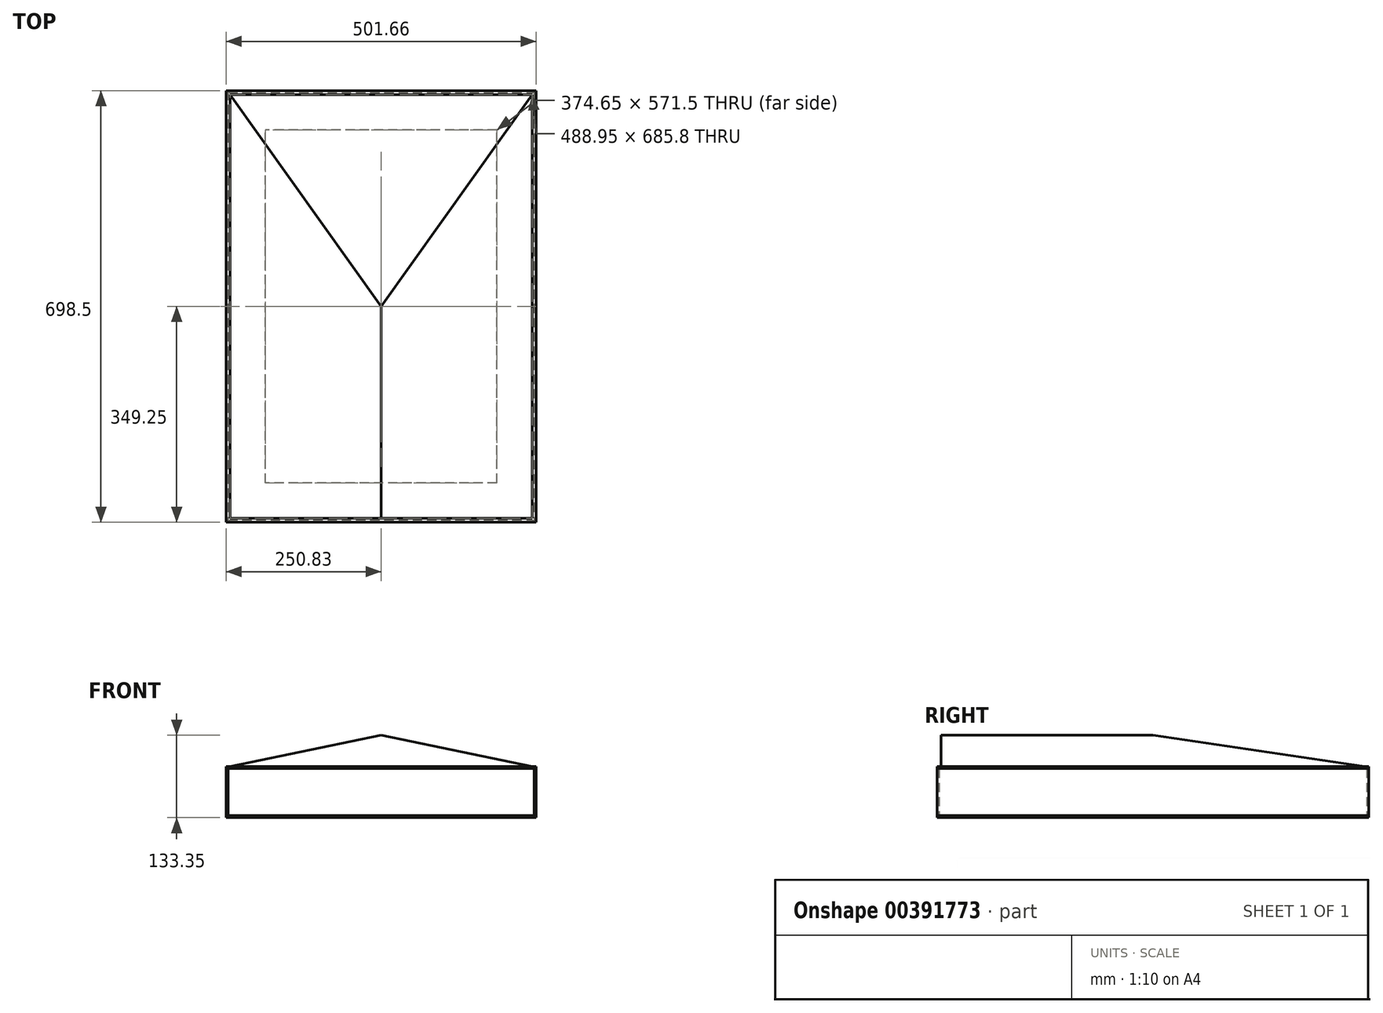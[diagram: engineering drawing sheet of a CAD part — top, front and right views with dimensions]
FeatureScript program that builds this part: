
annotation { "Feature Type Name" : "Feature", "Feature Type Description" : "" }
export const myFeature = defineFeature(function(context is Context, id is Id, definition is map)
    precondition{}
    {
        {
            var Q0;
            Q0=qCreatedBy(makeId("Top.planeOp"),FACE);
            var sketch = newSketch(context, id + "F0", { "sketchPlane" : qUnion([Q0])});
            skLineSegment(sketch, "E0.bottom", {"start": v(225.42, -323.85) * mm, "end": v(-225.43, -323.85) * mm});
            skLineSegment(sketch, "E0.top", {"start": v(225.43, 323.85) * mm, "end": v(-225.42, 323.85) * mm});
            skLineSegment(sketch, "E0.left", {"start": v(225.42, -323.85) * mm, "end": v(225.43, 323.85) * mm});
            skLineSegment(sketch, "E0.right", {"start": v(-225.43, -323.85) * mm, "end": v(-225.42, 323.85) * mm});
            skPoint(sketch, "E0.middle", {"position": v(0, 0) * mm});
            skLineSegment(sketch, "E1.0", {"start": v(-187.33, -285.75) * mm, "end": v(-187.32, 285.75) * mm});
            skLineSegment(sketch, "E1.1", {"start": v(187.32, -285.75) * mm, "end": v(-187.33, -285.75) * mm});
            skLineSegment(sketch, "E1.2", {"start": v(187.32, -285.75) * mm, "end": v(187.33, 285.75) * mm});
            skLineSegment(sketch, "E1.3", {"start": v(187.33, 285.75) * mm, "end": v(-187.32, 285.75) * mm});
            skLineSegment(sketch, "E2.0", {"start": v(-250.83, -349.25) * mm, "end": v(-250.83, 349.25) * mm});
            skLineSegment(sketch, "E2.1", {"start": v(250.83, -349.25) * mm, "end": v(-250.83, -349.25) * mm});
            skLineSegment(sketch, "E2.2", {"start": v(250.83, -349.25) * mm, "end": v(250.83, 349.25) * mm});
            skLineSegment(sketch, "E2.3", {"start": v(250.83, 349.25) * mm, "end": v(-250.83, 349.25) * mm});
            skSolve(sketch);
        }
        {
            var Q0;
            Q0 = qSketchRegion(id + "Ful7OC0vkHjbYUr_0", true);
            var Q1;
            Q1=makeQuery(id+"F0.imprint","IMPRINT",FACE,{"disambiguationData":[TD([[makeQuery(id+"F0.imprint","IMPRINT",EDGE,{"derivedFrom":sQuery(id+"F0.wireOp",EDGE,"E0.bottom")}),1.0]])]});
            var Q2;
            Q2=makeQuery(id+"F0.imprint","IMPRINT",FACE,{"disambiguationData":[TD([[makeQuery(id+"F0.imprint","IMPRINT",EDGE,{"derivedFrom":sQuery(id+"F0.wireOp",EDGE,"E0.bottom")}),-1.0]])]});
            extrude(context, id + "F1", {"entities" : qUnion([Q0, Q1, Q2]), "depth" : 3.17 * mm});
        }
        {
            var Q0;
            Q0=makeQuery(id+"F1.opExtrude","CAP_FACE",FACE,{"disambiguationData":[OSD([sQuery(id+"F0.wireOp",EDGE,"E1.0"),sQuery(id+"F0.wireOp",EDGE,"E1.1"),sQuery(id+"F0.wireOp",EDGE,"E1.2"),sQuery(id+"F0.wireOp",EDGE,"E1.3"),sQuery(id+"F0.wireOp",EDGE,"E2.0"),sQuery(id+"F0.wireOp",EDGE,"E2.1"),sQuery(id+"F0.wireOp",EDGE,"E2.2"),sQuery(id+"F0.wireOp",EDGE,"E2.3")])],"isStart":false});
            var sketch = newSketch(context, id + "F2", { "sketchPlane" : qUnion([Q0])});
            skLineSegment(sketch, "E3.bottom", {"start": v(-250.83, 349.25) * mm, "end": v(-247.65, 349.25) * mm});
            skLineSegment(sketch, "E3.top", {"start": v(-250.83, -349.25) * mm, "end": v(-247.65, -349.25) * mm});
            skLineSegment(sketch, "E3.left", {"start": v(-250.83, 349.25) * mm, "end": v(-250.83, -349.25) * mm});
            skLineSegment(sketch, "E3.right", {"start": v(-247.65, 349.25) * mm, "end": v(-247.65, -349.25) * mm});
            skSolve(sketch);
        }
        {
            var Q0;
            Q0 = qSketchRegion(id + "F2", true);
            extrude(context, id + "F3", {"entities" : qUnion([Q0]), "depth" : 76.2 * mm});
        }
        {
            var Q0;
            Q0=makeQuery(id+"F3.opExtrude","SWEPT_BODY",BODY,{"disambiguationData":[OSD([sQuery(id+"F2.wireOp",EDGE,"E3.bottom"),sQuery(id+"F2.wireOp",EDGE,"E3.top"),sQuery(id+"F2.wireOp",EDGE,"E3.left"),sQuery(id+"F2.wireOp",EDGE,"E3.right")])]});
            var Q1;
            Q1=qCreatedBy(makeId("Right.planeOp"),FACE);
            mirror(context, id + "F4", {"entities" : qUnion([Q0]), "mirrorPlane" : qUnion([Q1])});
        }
        {
            var Q0;
            Q0=makeQuery(id+"F1.opExtrude","CAP_FACE",FACE,{"disambiguationData":[OSD([sQuery(id+"F0.wireOp",EDGE,"E1.0"),sQuery(id+"F0.wireOp",EDGE,"E1.1"),sQuery(id+"F0.wireOp",EDGE,"E1.2"),sQuery(id+"F0.wireOp",EDGE,"E1.3"),sQuery(id+"F0.wireOp",EDGE,"E2.0"),sQuery(id+"F0.wireOp",EDGE,"E2.1"),sQuery(id+"F0.wireOp",EDGE,"E2.2"),sQuery(id+"F0.wireOp",EDGE,"E2.3")])],"isStart":false});
            var sketch = newSketch(context, id + "F5", { "sketchPlane" : qUnion([Q0])});
            skLineSegment(sketch, "E4.bottom", {"start": v(-247.65, -349.25) * mm, "end": v(247.65, -349.25) * mm});
            skLineSegment(sketch, "E4.top", {"start": v(-247.65, -346.08) * mm, "end": v(247.65, -346.08) * mm});
            skLineSegment(sketch, "E4.left", {"start": v(-247.65, -349.25) * mm, "end": v(-247.65, -346.08) * mm});
            skLineSegment(sketch, "E4.right", {"start": v(247.65, -349.25) * mm, "end": v(247.65, -346.08) * mm});
            skSolve(sketch);
        }
        {
            var Q0;
            Q0 = qSketchRegion(id + "F5", true);
            var Q1;
            Q1=makeQuery(id+"F4.opPattern","COPY",FACE,{"derivedFrom":makeQuery(id+"F3.opExtrude","CAP_FACE",FACE,{"disambiguationData":[OSD([sQuery(id+"F2.wireOp",EDGE,"E3.bottom"),sQuery(id+"F2.wireOp",EDGE,"E3.top"),sQuery(id+"F2.wireOp",EDGE,"E3.left"),sQuery(id+"F2.wireOp",EDGE,"E3.right")])],"isStart":false}),"instanceName":"1"});
            extrude(context, id + "F6", {"entities" : qUnion([Q0]), "endBound" : BoundingType.UP_TO_SURFACE, "endBoundEntityFace" : qUnion([Q1]), "depth" : 25.4 * mm});
        }
        {
            var Q0;
            Q0=makeQuery(id+"F6.opExtrude","SWEPT_BODY",BODY,{"disambiguationData":[OSD([sQuery(id+"F5.wireOp",EDGE,"E4.bottom"),sQuery(id+"F5.wireOp",EDGE,"E4.top"),sQuery(id+"F5.wireOp",EDGE,"E4.left"),sQuery(id+"F5.wireOp",EDGE,"E4.right")])]});
            var Q1;
            Q1=qCreatedBy(makeId("Front.planeOp"),FACE);
            mirror(context, id + "F7", {"entities" : qUnion([Q0]), "mirrorPlane" : qUnion([Q1])});
        }
        {
            var Q0;
            Q0=makeQuery(id+"F3.opExtrude","CAP_FACE",FACE,{"disambiguationData":[OSD([sQuery(id+"F2.wireOp",EDGE,"E3.bottom"),sQuery(id+"F2.wireOp",EDGE,"E3.top"),sQuery(id+"F2.wireOp",EDGE,"E3.left"),sQuery(id+"F2.wireOp",EDGE,"E3.right")])],"isStart":false});
            var sketch = newSketch(context, id + "F8", { "sketchPlane" : qUnion([Q0])});
            skLineSegment(sketch, "E5.bottom", {"start": v(-250.83, -349.25) * mm, "end": v(250.82, -349.25) * mm});
            skLineSegment(sketch, "E5.top", {"start": v(-250.83, 349.25) * mm, "end": v(250.83, 349.25) * mm});
            skLineSegment(sketch, "E5.left", {"start": v(-250.83, -349.25) * mm, "end": v(-250.83, 349.25) * mm});
            skLineSegment(sketch, "E5.right", {"start": v(250.83, -349.25) * mm, "end": v(250.83, 349.25) * mm});
            skLineSegment(sketch, "E6.bottom", {"start": v(-244.48, -342.9) * mm, "end": v(244.48, -342.9) * mm});
            skLineSegment(sketch, "E6.top", {"start": v(-244.48, 342.9) * mm, "end": v(244.48, 342.9) * mm});
            skLineSegment(sketch, "E6.left", {"start": v(-244.48, -342.9) * mm, "end": v(-244.48, 342.9) * mm});
            skLineSegment(sketch, "E6.right", {"start": v(244.48, -342.9) * mm, "end": v(244.48, 342.9) * mm});
            skPoint(sketch, "E6.middle", {"position": v(0, 0) * mm});
            skSolve(sketch);
        }
        {
            var Q0;
            Q0 = qSketchRegion(id + "F8", true);
            extrude(context, id + "F9", {"entities" : qUnion([Q0]), "depth" : 3.17 * mm});
        }
        {
            var Q0;
            Q0=makeQuery(id+"F9.opExtrude","SWEPT_FACE",FACE,{"disambiguationData":[OSD([sQuery(id+"F8.wireOp",EDGE,"E6.top")])]});
            var sketch = newSketch(context, id + "F10", { "sketchPlane" : qUnion([Q0])});
            skLineSegment(sketch, "E7", {"start": v(-244.48, 82.55) * mm, "end": v(0, 133.35) * mm});
            skLineSegment(sketch, "E8", {"start": v(0, 133.35) * mm, "end": v(244.48, 82.55) * mm});
            skLineSegment(sketch, "E9", {"start": v(244.48, 82.55) * mm, "end": v(-244.48, 82.55) * mm});
            skLineSegment(sketch, "E10", {"start": v(0, 133.35) * mm, "end": v(0, 82.55) * mm});
            skSolve(sketch);
        }
        {
            var Q0;
            Q0 = qSketchRegion(id + "F10", true);
            var Q1;
            Q1=makeQuery(id+"F9.opExtrude","SWEPT_FACE",FACE,{"disambiguationData":[OSD([sQuery(id+"F8.wireOp",EDGE,"E6.bottom")])]});
            extrude(context, id + "F11", {"entities" : qUnion([Q0]), "endBound" : BoundingType.UP_TO_SURFACE, "endBoundEntityFace" : qUnion([Q1]), "depth" : 25.4 * mm});
        }
        {
            var Q0;
            Q0=makeQuery(id+"F9.opExtrude","SWEPT_FACE",FACE,{"disambiguationData":[OSD([sQuery(id+"F8.wireOp",EDGE,"E5.right")])]});
            var sketch = newSketch(context, id + "F12", { "sketchPlane" : qUnion([Q0])});
            skLineSegment(sketch, "E11", {"start": v(342.9, 82.55) * mm, "end": v(0, 133.35) * mm});
            skLineSegment(sketch, "E12", {"start": v(0, 133.35) * mm, "end": v(342.9, 133.35) * mm});
            skLineSegment(sketch, "E13", {"start": v(342.9, 133.35) * mm, "end": v(342.9, 82.55) * mm});
            skLineSegment(sketch, "E14", {"start": v(0, 133.35) * mm, "end": v(0, 82.55) * mm, "construction": true});
            skSolve(sketch);
        }
        {
            var Q0;
            Q0 = qSketchRegion(id + "F12", true);
            extrude(context, id + "F13", {"entities" : qUnion([Q0]), "operationType" : NewBodyOperationType.REMOVE, "endBound" : BoundingType.THROUGH_ALL, "oppositeDirection" : true, "depth" : 25.4 * mm});
        }
    });
